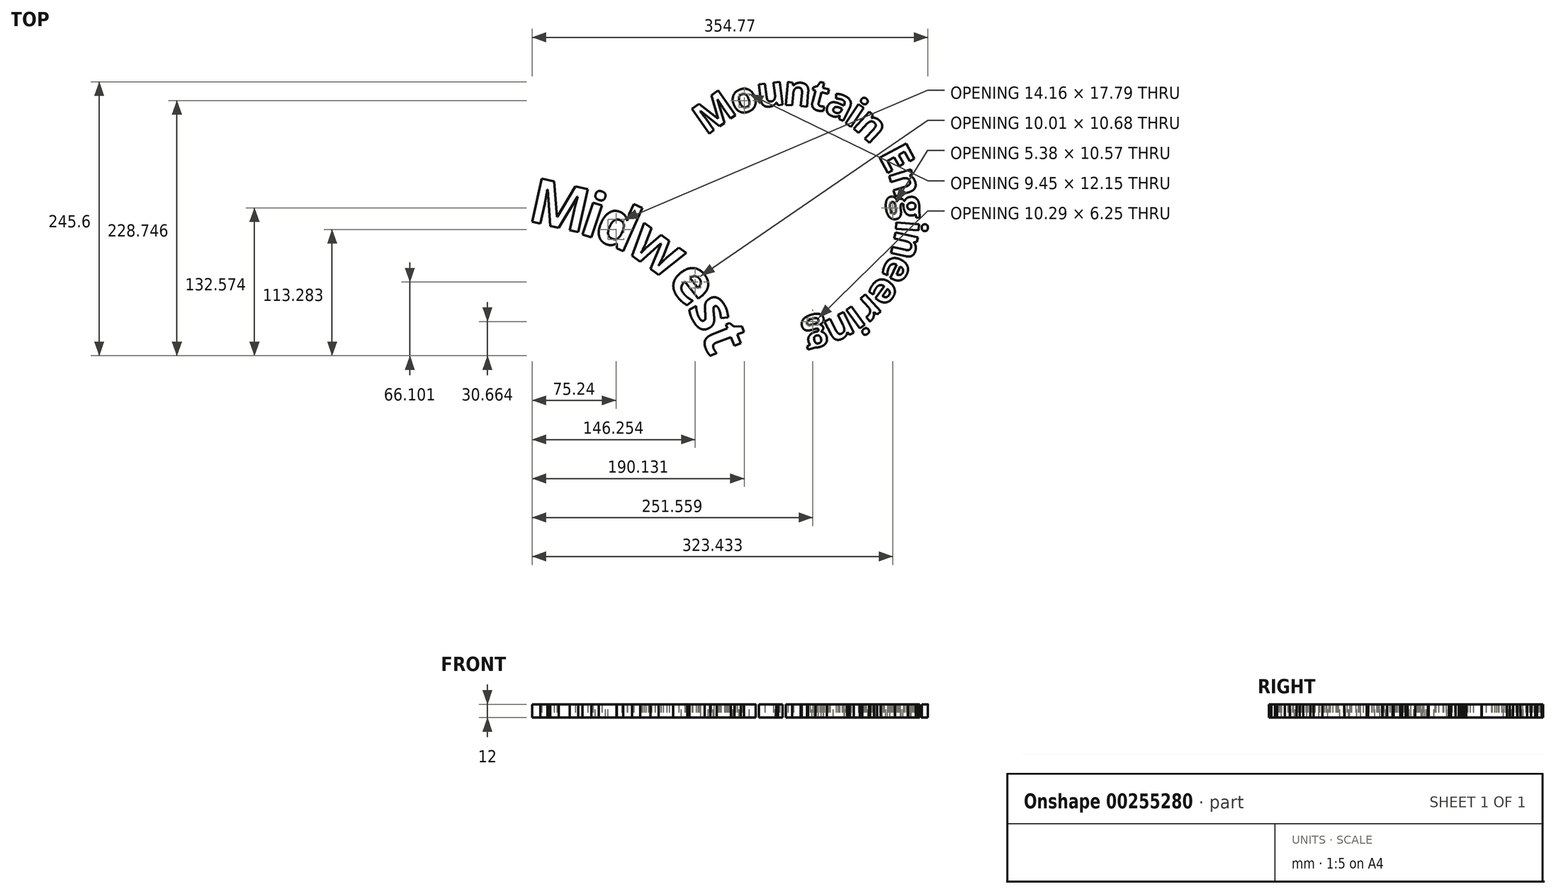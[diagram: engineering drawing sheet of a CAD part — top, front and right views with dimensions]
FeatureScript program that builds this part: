
annotation { "Feature Type Name" : "Feature", "Feature Type Description" : "" }
export const myFeature = defineFeature(function(context is Context, id is Id, definition is map)
    precondition{}
    {
        {
            var Q0;
            Q0=qCreatedBy(makeId("Top.planeOp"),FACE);
            var sketch = newSketch(context, id + "F0", { "sketchPlane" : qUnion([Q0])});
            skText(sketch, "E0", { "text": "M", "fontName": "OpenSans-Bold.ttf"});
            skText(sketch, "E1", { "text": "i", "fontName": "OpenSans-Bold.ttf"});
            skText(sketch, "E2", { "text": "d", "fontName": "OpenSans-Bold.ttf"});
            skText(sketch, "E3", { "text": "w", "fontName": "OpenSans-Bold.ttf"});
            skText(sketch, "E4", { "text": "e", "fontName": "OpenSans-Bold.ttf"});
            skText(sketch, "E5", { "text": "s", "fontName": "OpenSans-Bold.ttf"});
            skText(sketch, "E6", { "text": "t", "fontName": "OpenSans-Bold.ttf"});
            skText(sketch, "E7", { "text": "o", "fontName": "OpenSans-Bold.ttf"});
            skText(sketch, "E8", { "text": "u", "fontName": "OpenSans-Bold.ttf"});
            skText(sketch, "E9", { "text": "n", "fontName": "OpenSans-Bold.ttf"});
            skText(sketch, "E10", { "text": "M", "fontName": "OpenSans-Bold.ttf"});
            skText(sketch, "E11", { "text": "t", "fontName": "OpenSans-Bold.ttf"});
            skText(sketch, "E12", { "text": "a", "fontName": "OpenSans-Bold.ttf"});
            skText(sketch, "E13", { "text": "i", "fontName": "OpenSans-Bold.ttf"});
            skText(sketch, "E14", { "text": "n", "fontName": "OpenSans-Bold.ttf"});
            skText(sketch, "E15", { "text": "E", "fontName": "OpenSans-Bold.ttf"});
            skText(sketch, "E16", { "text": "n", "fontName": "OpenSans-Bold.ttf"});
            skText(sketch, "E17", { "text": "g", "fontName": "OpenSans-Bold.ttf"});
            skText(sketch, "E18", { "text": "i", "fontName": "OpenSans-Bold.ttf"});
            skText(sketch, "E19", { "text": "n", "fontName": "OpenSans-Bold.ttf"});
            skText(sketch, "E20", { "text": "e", "fontName": "OpenSans-Bold.ttf"});
            skText(sketch, "E21", { "text": "e", "fontName": "OpenSans-Bold.ttf"});
            skText(sketch, "E22", { "text": "r", "fontName": "OpenSans-Bold.ttf"});
            skText(sketch, "E23", { "text": "i", "fontName": "OpenSans-Bold.ttf"});
            skText(sketch, "E24", { "text": "n", "fontName": "OpenSans-Bold.ttf"});
            skText(sketch, "E25", { "text": "g", "fontName": "OpenSans-Bold.ttf"});
            skFitSpline(sketch, "E26", {"points": [v(-509.02, -128.55) * mm, v(-114.69, -51.63) * mm, v(0, -335.04) * mm, v(145.58, -82.27) * mm], "startDerivative": vector(-305.8, 1050.7) * mm, "endDerivative": vector(-1254.4, 814.2) * mm});
            skLineSegment(sketch, "E27", {"start": v(-199.46, -59.93) * mm, "end": v(-185.48, -14.72) * mm, "construction": true});
            skLineSegment(sketch, "E28", {"start": v(-189.32, -63.34) * mm, "end": v(-173.16, -18.86) * mm, "construction": true});
            skLineSegment(sketch, "E29", {"start": v(-145, -31.24) * mm, "end": v(-122.88, 10.6) * mm, "construction": true});
            skLineSegment(sketch, "E30", {"start": v(-107.32, -58.47) * mm, "end": v(-73.86, -25) * mm, "construction": true});
            skLineSegment(sketch, "E31", {"start": v(-88.32, -82.03) * mm, "end": v(-48.65, -56.21) * mm, "construction": true});
            skLineSegment(sketch, "E32", {"start": v(-76.1, -104.33) * mm, "end": v(-119.1, -124.08) * mm, "construction": true});
            const initialGuessF0  = {"E0": [-0.23143, -0.00341, 0.97535, -0.22069, 0.04], "E1": [-0.18545, -0.01465, 0.9481, -0.31795, 0.04], "E2": [-0.17299, -0.01838, 0.91607, -0.40102, 0.04], "E3": [-0.14423, -0.02979, 0.8135, -0.58156, 0.04], "E4": [-0.10675, -0.0579, 0.62703, -0.779, 0.04], "E5": [-0.08791, -0.08176, 0.47934, -0.87763, 0.04], "E6": [-0.07583, -0.1042, 0.36744, -0.93005, 0.04], "E7": [-0.04391, 0.09049, 0.94134, 0.33746, 0.02708], "E8": [-0.02358, 0.09779, 0.9918, 0.1278, 0.02708], "E9": [-0.00198, 0.10058, 0.99601, -0.08924, 0.02708], "E10": [-0.0705, 0.07271, 0.81915, 0.57358, 0.02708], "E11": [0.01977, 0.09832, 0.96274, -0.27042, 0.02708], "E12": [0.0344, 0.09443, 0.90115, -0.43352, 0.02708], "E13": [0.0521, 0.08546, 0.83012, -0.55759, 0.02708], "E14": [0.0597, 0.08096, 0.73545, -0.67758, 0.02708], "E15": [0.08348, 0.05585, 0.47567, -0.87962, 0.02708], "E16": [0.09259, 0.03934, 0.2886, -0.95745, 0.02708], "E17": [0.09885, 0.01837, 0.07995, -0.9968, 0.02708], "E18": [0.10007, -0.00237, -0.06756, -0.99772, 0.02708], "E19": [0.09997, -0.0112, -0.21883, -0.97576, 0.02708], "E20": [0.09512, -0.03254, -0.41897, -0.908, 0.02708], "E21": [0.08648, -0.05125, -0.5953, -0.8035, 0.02708], "E22": [0.07407, -0.06768, -0.73224, -0.68105, 0.02708], "E23": [0.062, -0.07859, -0.81158, -0.58425, 0.02708], "E24": [0.05513, -0.08415, -0.89114, -0.45374, 0.02708], "E25": [0.0356, -0.09403, -0.96684, -0.25537, 0.02708]};
            skSetInitialGuess(sketch, initialGuessF0);
            skSolve(sketch);
        }
        {
            var Q0;
            Q0=qSketchRegion(id+"F0",true);
            extrude(context, id + "F1", {"entities" : qUnion([Q0]), "depth" : 10 * mm, "hasSecondDirection" : true, "secondDirectionOppositeDirection" : true, "secondDirectionDepth" : 2 * mm});
        }
    });
